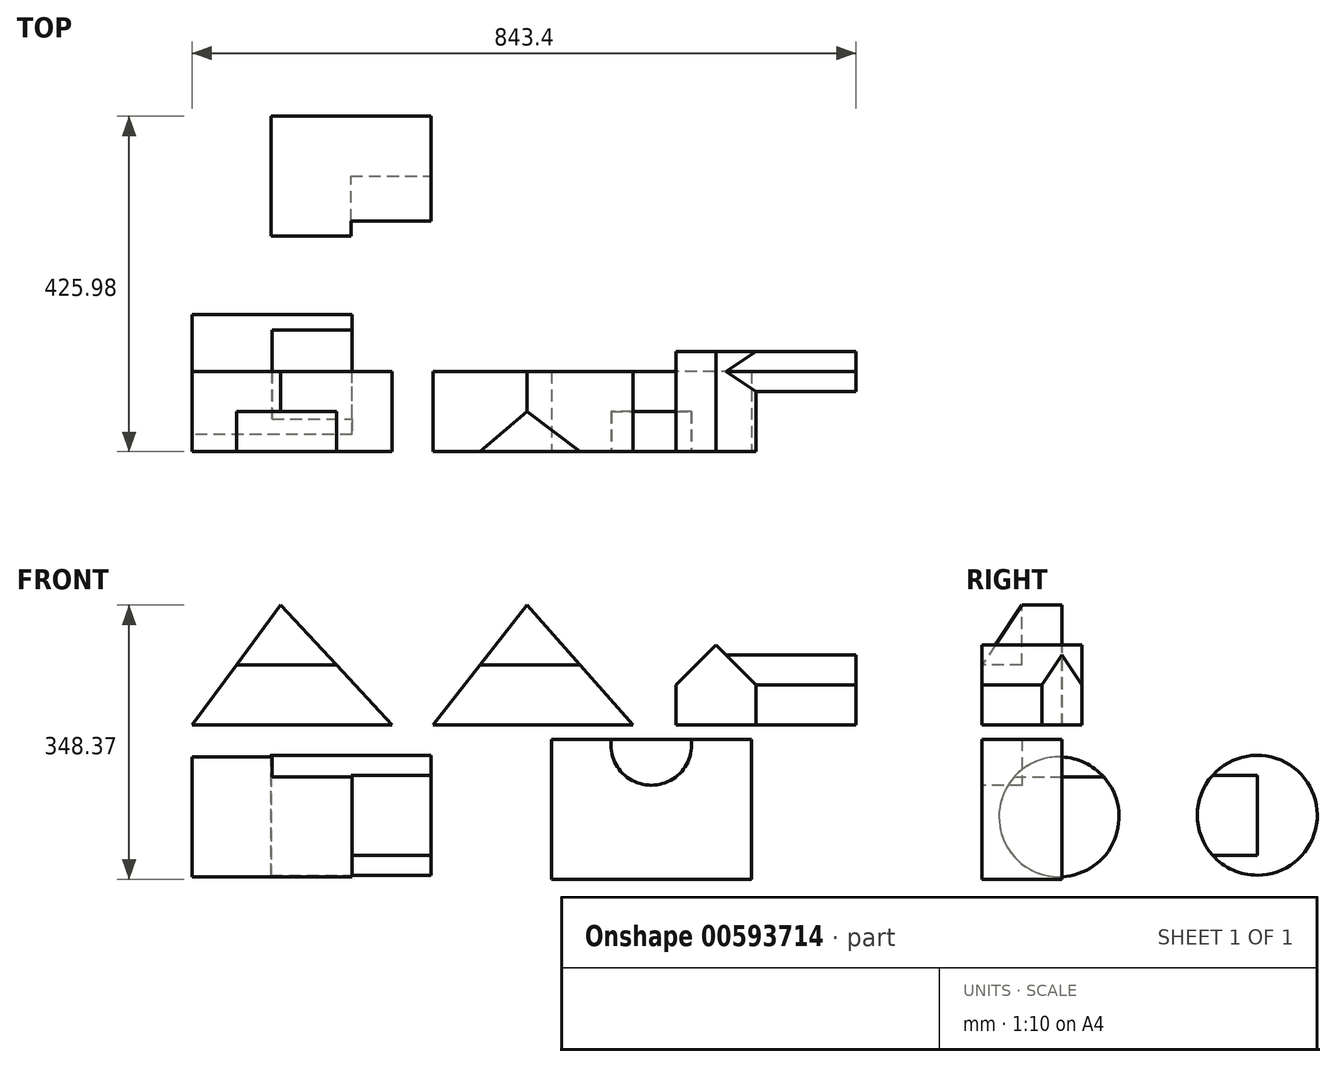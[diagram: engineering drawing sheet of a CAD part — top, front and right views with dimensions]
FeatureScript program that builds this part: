
annotation { "Feature Type Name" : "Feature", "Feature Type Description" : "" }
export const myFeature = defineFeature(function(context is Context, id is Id, definition is map)
    precondition{}
    {
        {
            var Q0;
            Q0=qCreatedBy(makeId("Front.planeOp"),FACE);
            var sketch = newSketch(context, id + "F0", { "sketchPlane" : qUnion([Q0])});
            skLineSegment(sketch, "E0", {"start": v(0, 0) * mm, "end": v(254, 0) * mm});
            skLineSegment(sketch, "E1", {"start": v(254, 0) * mm, "end": v(112.57, 152.4) * mm});
            skLineSegment(sketch, "E2", {"start": v(112.57, 152.4) * mm, "end": v(0, 0) * mm});
            skSolve(sketch);
        }
        {
            var Q0;
            Q0=makeQuery(id+"F0.imprint","IMPRINT",FACE,{"disambiguationData":[TD([[makeQuery(id+"F0.imprint","IMPRINT",EDGE,{"derivedFrom":sQuery(id+"F0.wireOp",EDGE,"E0")}),1.0]])]});
            extrude(context, id + "F1", {"entities" : qUnion([Q0]), "oppositeDirection" : true, "depth" : 101.6 * mm, "offsetDistance" : 25.4 * mm});
        }
        {
            var Q0;
            Q0=makeQuery(id+"F1.opExtrude","CAP_FACE",FACE,{"disambiguationData":[OSD([sQuery(id+"F0.wireOp",EDGE,"E0"),sQuery(id+"F0.wireOp",EDGE,"E1"),sQuery(id+"F0.wireOp",EDGE,"E2")])],"isStart":true});
            var sketch = newSketch(context, id + "F2", { "sketchPlane" : qUnion([Q0])});
            skLineSegment(sketch, "E3", {"start": v(112.57, 152.4) * mm, "end": v(56.29, 76.2) * mm});
            skLineSegment(sketch, "E4", {"start": v(56.29, 76.2) * mm, "end": v(183.29, 76.2) * mm});
            skLineSegment(sketch, "E5", {"start": v(183.29, 76.2) * mm, "end": v(112.57, 152.4) * mm});
            skSolve(sketch);
        }
        {
            var Q0;
            Q0 = qSketchRegion(id + "F2", true);
            extrude(context, id + "F3", {"entities" : qUnion([Q0]), "operationType" : NewBodyOperationType.ADD, "oppositeDirection" : true, "depth" : 50.8 * mm, "offsetDistance" : 25.4 * mm});
        }
        {
            var Q0;
            Q0=makeQuery(id+"F1.opExtrude","CAP_FACE",FACE,{"disambiguationData":[OSD([sQuery(id+"F0.wireOp",EDGE,"E0"),sQuery(id+"F0.wireOp",EDGE,"E1"),sQuery(id+"F0.wireOp",EDGE,"E2")])],"isStart":true});
            var sketch = newSketch(context, id + "F4", { "sketchPlane" : qUnion([Q0])});
            skLineSegment(sketch, "E6", {"start": v(112.57, 152.4) * mm, "end": v(56.29, 76.2) * mm});
            skLineSegment(sketch, "E7", {"start": v(56.29, 76.2) * mm, "end": v(183.29, 76.2) * mm});
            skLineSegment(sketch, "E8", {"start": v(183.29, 76.2) * mm, "end": v(112.57, 152.4) * mm});
            skSolve(sketch);
        }
        {
            var Q0;
            Q0=makeQuery(id+"F4.imprint","IMPRINT",FACE,{"disambiguationData":[TD([[makeQuery(id+"F4.imprint","IMPRINT",EDGE,{"derivedFrom":sQuery(id+"F4.wireOp",EDGE,"E6")}),1.0]])]});
            extrude(context, id + "F5", {"entities" : qUnion([Q0]), "operationType" : NewBodyOperationType.REMOVE, "oppositeDirection" : true, "depth" : 50.8 * mm, "offsetDistance" : 25.4 * mm});
        }
        {
            var Q0;
            Q0=qCreatedBy(makeId("Front.planeOp"),FACE);
            var sketch = newSketch(context, id + "F6", { "sketchPlane" : qUnion([Q0])});
            skLineSegment(sketch, "E9", {"start": v(305.97, 0) * mm, "end": v(559.97, 0) * mm});
            skLineSegment(sketch, "E10", {"start": v(559.97, 0) * mm, "end": v(425.43, 152.4) * mm});
            skLineSegment(sketch, "E11", {"start": v(425.43, 152.4) * mm, "end": v(305.97, 0) * mm});
            skSolve(sketch);
        }
        {
            var Q0;
            Q0 = qSketchRegion(id + "F6", true);
            extrude(context, id + "F7", {"entities" : qUnion([Q0]), "oppositeDirection" : true, "depth" : 101.6 * mm, "offsetDistance" : 25.4 * mm});
        }
        {
            var Q0;
            Q0=qCreatedBy(makeId("Right.planeOp"),FACE);
            cPlane(context, id + "F8", {"entities" : qUnion([Q0]), "cplaneType" : CPlaneType.OFFSET, "offset" : 303.28 * mm, "width" : 152.4 * mm, "height" : 152.4 * mm});
        }
        {
            var Q0;
            Q0=qCreatedBy(id+"F8.planeOp",FACE);
            var sketch = newSketch(context, id + "F9", { "sketchPlane" : qUnion([Q0])});
            skLineSegment(sketch, "E12", {"start": v(0, 76.2) * mm, "end": v(50.8, 152.4) * mm});
            skLineSegment(sketch, "E13", {"start": v(50.8, 152.4) * mm, "end": v(0, 152.4) * mm});
            skLineSegment(sketch, "E14", {"start": v(0, 152.4) * mm, "end": v(0, 76.2) * mm});
            skSolve(sketch);
        }
        {
            var Q0;
            Q0=makeQuery(id+"F9.imprint","IMPRINT",FACE,{"disambiguationData":[TD([[makeQuery(id+"F9.imprint","IMPRINT",EDGE,{"derivedFrom":sQuery(id+"F9.wireOp",EDGE,"E12")}),1.0]])]});
            extrude(context, id + "F10", {"entities" : qUnion([Q0]), "operationType" : NewBodyOperationType.REMOVE, "depth" : 279.4 * mm, "offsetDistance" : 25.4 * mm});
        }
        {
            var Q0;
            Q0=qCreatedBy(makeId("Front.planeOp"),FACE);
            var sketch = newSketch(context, id + "F11", { "sketchPlane" : qUnion([Q0])});
            skLineSegment(sketch, "E15", {"start": v(614.8, 0) * mm, "end": v(716.4, 0) * mm});
            skLineSegment(sketch, "E16", {"start": v(716.4, 0) * mm, "end": v(716.4, 50.8) * mm});
            skLineSegment(sketch, "E17", {"start": v(716.4, 50.8) * mm, "end": v(665.6, 101.6) * mm});
            skLineSegment(sketch, "E18", {"start": v(665.6, 101.6) * mm, "end": v(614.8, 50.8) * mm});
            skLineSegment(sketch, "E19", {"start": v(614.8, 50.8) * mm, "end": v(614.8, 0) * mm});
            skSolve(sketch);
        }
        {
            var Q0;
            Q0=makeQuery(id+"F11.imprint","IMPRINT",FACE,{"disambiguationData":[TD([[makeQuery(id+"F11.imprint","IMPRINT",EDGE,{"derivedFrom":sQuery(id+"F11.wireOp",EDGE,"E15")}),1.0]])]});
            extrude(context, id + "F12", {"entities" : qUnion([Q0]), "oppositeDirection" : true, "depth" : 127 * mm, "offsetDistance" : 25.4 * mm});
        }
        {
            var Q0;
            Q0=makeQuery(id+"F12.opExtrude","SWEPT_FACE",FACE,{"disambiguationData":[OSD([sQuery(id+"F11.wireOp",EDGE,"E16")])]});
            cPlane(context, id + "F13", {"entities" : qUnion([Q0]), "cplaneType" : CPlaneType.OFFSET, "offset" : 127 * mm, "width" : 152.4 * mm, "height" : 152.4 * mm});
        }
        {
            var Q0;
            Q0=qCreatedBy(id+"F13.planeOp",FACE);
            var sketch = newSketch(context, id + "F14", { "sketchPlane" : qUnion([Q0])});
            skLineSegment(sketch, "E20", {"start": v(127, 0) * mm, "end": v(127, 50.8) * mm});
            skLineSegment(sketch, "E21", {"start": v(127, 50.8) * mm, "end": v(76.2, 50.8) * mm});
            skLineSegment(sketch, "E22", {"start": v(76.2, 50.8) * mm, "end": v(76.2, 0) * mm});
            skLineSegment(sketch, "E23", {"start": v(76.2, 0) * mm, "end": v(127, 0) * mm});
            skLineSegment(sketch, "E24", {"start": v(76.2, 50.8) * mm, "end": v(101.6, 88.9) * mm});
            skLineSegment(sketch, "E25", {"start": v(101.6, 88.9) * mm, "end": v(127, 50.8) * mm});
            skSolve(sketch);
        }
        {
            var Q0;
            Q0=makeQuery(id+"F14.imprint","IMPRINT",FACE,{"disambiguationData":[TD([[makeQuery(id+"F14.imprint","IMPRINT",EDGE,{"derivedFrom":sQuery(id+"F14.wireOp",EDGE,"E20")}),1.0]])]});
            var Q1;
            Q1=makeQuery(id+"F14.imprint","IMPRINT",FACE,{"disambiguationData":[TD([[makeQuery(id+"F14.imprint","IMPRINT",EDGE,{"derivedFrom":sQuery(id+"F14.wireOp",EDGE,"E21")}),-1.0]])]});
            extrude(context, id + "F15", {"entities" : qUnion([Q0, Q1]), "operationType" : NewBodyOperationType.ADD, "endBound" : BoundingType.UP_TO_NEXT, "oppositeDirection" : true, "depth" : 25.4 * mm, "offsetDistance" : 25.4 * mm});
        }
        {
            var Q0;
            Q0=qCreatedBy(makeId("Right.planeOp"),FACE);
            var sketch = newSketch(context, id + "F16", { "sketchPlane" : qUnion([Q0])});
            skCircle(sketch, "E26", {"center": v(97.85, -116.78) * mm, "radius": 76.2 * mm});
            skSolve(sketch);
        }
        {
            var Q0;
            Q0 = qSketchRegion(id + "F16", true);
            extrude(context, id + "F17", {"entities" : qUnion([Q0]), "depth" : 203.2 * mm, "offsetDistance" : 25.4 * mm});
        }
        {
            var Q0;
            Q0=makeQuery(id+"F17.opExtrude","CAP_FACE",FACE,{"disambiguationData":[OSD([sQuery(id+"F16.wireOp",EDGE,"E26")])],"isStart":false});
            var sketch = newSketch(context, id + "F18", { "sketchPlane" : qUnion([Q0])});
            skLineSegment(sketch, "E27", {"start": v(41.06, -65.98) * mm, "end": v(154.65, -65.98) * mm});
            skSolve(sketch);
        }
        {
            var Q0;
            {var subQ0=sQuery(id+"F18.wireOp",EDGE,"E27");Q0=makeQuery(id+"F18.imprint","IMPRINT",FACE,{"disambiguationData":[TD([[makeQuery(id+"F18.imprint","IMPRINT",EDGE,{"derivedFrom":subQ0}),1.0]])]});}
            extrude(context, id + "F19", {"entities" : qUnion([Q0]), "operationType" : NewBodyOperationType.REMOVE, "oppositeDirection" : true, "depth" : 101.6 * mm, "offsetDistance" : 25.4 * mm});
        }
        {
            var Q0;
            Q0=qCreatedBy(id+"F8.planeOp",FACE);
            var sketch = newSketch(context, id + "F20", { "sketchPlane" : qUnion([Q0])});
            skCircle(sketch, "E28", {"center": v(349.78, -114.64) * mm, "radius": 76.2 * mm});
            skSolve(sketch);
        }
        {
            var Q0;
            Q0 = qSketchRegion(id + "F20", true);
            extrude(context, id + "F21", {"entities" : qUnion([Q0]), "oppositeDirection" : true, "depth" : 203.2 * mm, "offsetDistance" : 25.4 * mm});
        }
        {
            var Q0;
            Q0=makeQuery(id+"F21.opExtrude","CAP_FACE",FACE,{"disambiguationData":[OSD([sQuery(id+"F20.wireOp",EDGE,"E28")])],"isStart":true});
            var sketch = newSketch(context, id + "F22", { "sketchPlane" : qUnion([Q0])});
            skLineSegment(sketch, "E29", {"start": v(292.98, -63.84) * mm, "end": v(349.78, -63.84) * mm});
            skLineSegment(sketch, "E30", {"start": v(349.78, -63.84) * mm, "end": v(349.78, -165.44) * mm});
            skLineSegment(sketch, "E31", {"start": v(349.78, -165.44) * mm, "end": v(292.98, -165.44) * mm});
            skSolve(sketch);
        }
        {
            var Q0;
            Q0 = qSketchRegion(id + "F22", true);
            var Q1;
            {var subQ0=sQuery(id+"F22.wireOp",EDGE,"E29");Q1=makeQuery(id+"F22.imprint","IMPRINT",FACE,{"disambiguationData":[TD([[makeQuery(id+"F22.imprint","IMPRINT",EDGE,{"derivedFrom":subQ0}),-1.0]])]});}
            extrude(context, id + "F23", {"entities" : qUnion([Q0, Q1]), "operationType" : NewBodyOperationType.REMOVE, "oppositeDirection" : true, "depth" : 101.6 * mm, "offsetDistance" : 25.4 * mm});
        }
        {
            var Q0;
            Q0=qCreatedBy(makeId("Front.planeOp"),FACE);
            var sketch = newSketch(context, id + "F24", { "sketchPlane" : qUnion([Q0])});
            skLineSegment(sketch, "E32", {"start": v(456.26, -195.97) * mm, "end": v(710.26, -195.97) * mm});
            skLineSegment(sketch, "E33", {"start": v(710.26, -195.97) * mm, "end": v(710.26, -18.17) * mm});
            skLineSegment(sketch, "E34", {"start": v(710.26, -18.17) * mm, "end": v(456.26, -18.17) * mm});
            skLineSegment(sketch, "E35", {"start": v(456.26, -18.17) * mm, "end": v(456.26, -195.97) * mm});
            skSolve(sketch);
        }
        {
            var Q0;
            Q0 = qSketchRegion(id + "F24", true);
            extrude(context, id + "F25", {"entities" : qUnion([Q0]), "oppositeDirection" : true, "depth" : 101.6 * mm, "offsetDistance" : 25.4 * mm});
        }
        {
            var Q0;
            Q0=makeQuery(id+"F25.opExtrude","CAP_FACE",FACE,{"disambiguationData":[OSD([sQuery(id+"F24.wireOp",EDGE,"E32"),sQuery(id+"F24.wireOp",EDGE,"E33"),sQuery(id+"F24.wireOp",EDGE,"E34"),sQuery(id+"F24.wireOp",EDGE,"E35")])],"isStart":true});
            var sketch = newSketch(context, id + "F26", { "sketchPlane" : qUnion([Q0])});
            skCircle(sketch, "E36", {"center": v(583.26, -25.23) * mm, "radius": 51.29 * mm});
            skPoint(sketch, "E36.first.point", {"position": v(532.46, -18.17) * mm});
            skPoint(sketch, "E36.second.point", {"position": v(612.58, -67.32) * mm});
            skPoint(sketch, "E36.third.point", {"position": v(634.06, -32.3) * mm});
            skSolve(sketch);
        }
        {
            var Q0;
            {var subQ0=sQuery(id+"F26.wireOp",EDGE,"E36");var subQ1=makeQuery(id+"F25.opExtrude","CAP_EDGE",EDGE,{"disambiguationData":[OSD([sQuery(id+"F24.wireOp",EDGE,"E34")])],"isStart":true});var subQ2=makeQuery(id+"F26.imprint","INTERSECT",VERTEX,{"disambiguationData":[OD(0.0)],"derivedFrom":[subQ1,subQ0]});Q0=makeQuery(id+"F26.imprint","IMPRINT",FACE,{"disambiguationData":[TD([[makeQuery(id+"F26.imprint","IMPRINT",EDGE,{"disambiguationData":[TD([[subQ2,1.0]])],"derivedFrom":subQ0}),1.0]])]});}
            extrude(context, id + "F27", {"entities" : qUnion([Q0]), "operationType" : NewBodyOperationType.REMOVE, "oppositeDirection" : true, "depth" : 50.8 * mm, "offsetDistance" : 25.4 * mm});
        }
    });
